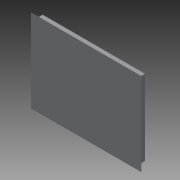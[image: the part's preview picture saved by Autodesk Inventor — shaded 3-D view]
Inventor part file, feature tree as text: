
AUTODESK INVENTOR PART (.ipt)
format: ipt  version: 2014 (Build 180170000, 170)  size: 83,456 bytes
history: native  units: mm
features: extrude x2, sketch x2, chamfer x1
ambient origin geometry x8: Origin, YZ Plane, XZ Plane, XY Plane, X Axis, Y Axis, Z Axis, Center Point
bodies: Solid1 (feature_tree)
feature tree (5):
  extrude  "Extrusion1"  Depth=19.6mm
  extrude  "Extrusion2"  Depth=1.0mm
  chamfer  "Chamfer1"  Distance=1.0mm
  sketch  "Sketch1"  dims[d0=26.6mm d1=19.6mm]
  sketch  "Sketch2"  dims[d2=1.0mm d3=0.0mm d4=1.0mm d5=1.0mm d6=1.0mm d7=0.0mm d8=1.0mm d9=2.0mm d10=45.0deg]
